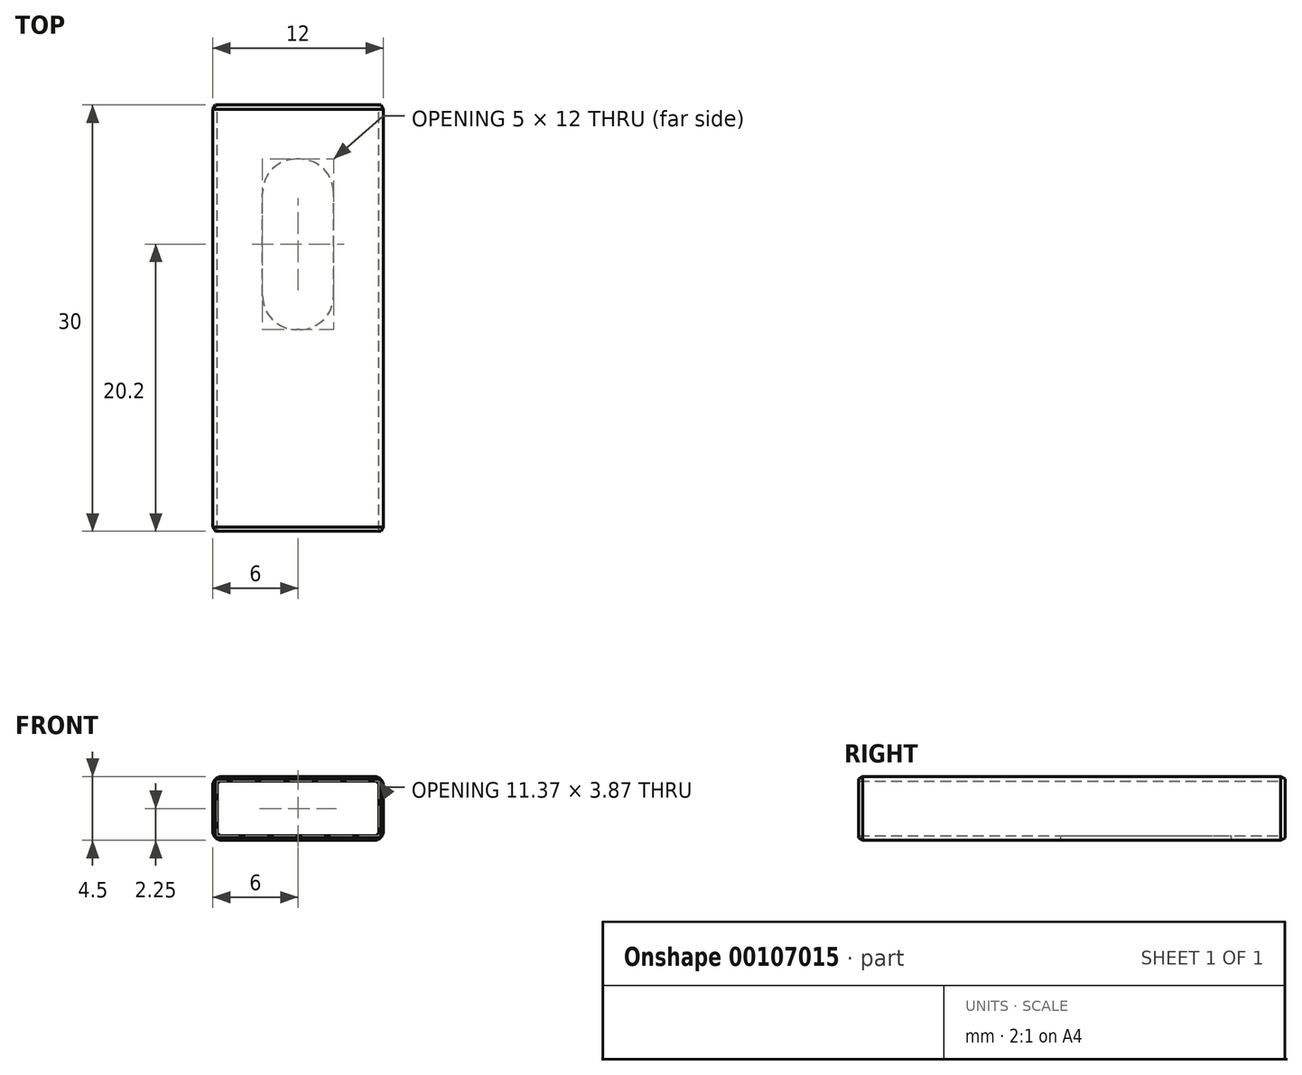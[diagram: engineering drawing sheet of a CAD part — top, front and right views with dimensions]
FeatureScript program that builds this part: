
annotation { "Feature Type Name" : "Feature", "Feature Type Description" : "" }
export const myFeature = defineFeature(function(context is Context, id is Id, definition is map)
    precondition{}
    {
        {
            var Q0;
            Q0=qCreatedBy(makeId("Front.planeOp"),FACE);
            var sketch = newSketch(context, id + "F0", { "sketchPlane" : qUnion([Q0])});
            skLineSegment(sketch, "E0.bottom", {"start": v(0.64, 0) * mm, "end": v(11.36, 0) * mm});
            skLineSegment(sketch, "E0.top", {"start": v(0.64, 4.5) * mm, "end": v(11.36, 4.5) * mm});
            skLineSegment(sketch, "E0.left", {"start": v(0, 0.64) * mm, "end": v(0, 3.86) * mm});
            skLineSegment(sketch, "E0.right", {"start": v(12, 0.64) * mm, "end": v(12, 3.86) * mm});
            skPoint(sketch, "E1.visualSharp", {"position": v(0, 4.5) * mm});
            skArc(sketch, "E1.filletArc", {"start": v(0.64, 4.5) * mm, "mid": v(0.19, 4.31) * mm, "end": v(0, 3.86) * mm});
            skPoint(sketch, "E2.visualSharp", {"position": v(12, 4.5) * mm});
            skArc(sketch, "E2.filletArc", {"start": v(12, 3.86) * mm, "mid": v(11.81, 4.31) * mm, "end": v(11.36, 4.5) * mm});
            skPoint(sketch, "E3.visualSharp", {"position": v(12, 0) * mm});
            skArc(sketch, "E3.filletArc", {"start": v(11.36, 0) * mm, "mid": v(11.81, 0.19) * mm, "end": v(12, 0.64) * mm});
            skPoint(sketch, "E4.visualSharp", {"position": v(0, 0) * mm});
            skArc(sketch, "E4.filletArc", {"start": v(0, 0.64) * mm, "mid": v(0.19, 0.19) * mm, "end": v(0.64, 0) * mm});
            skArc(sketch, "E5.0", {"start": v(0.64, 4.19) * mm, "mid": v(0.41, 4.09) * mm, "end": v(0.31, 3.86) * mm});
            skLineSegment(sketch, "E5.1", {"start": v(0.32, 0.64) * mm, "end": v(0.31, 3.86) * mm});
            skLineSegment(sketch, "E5.2", {"start": v(0.64, 4.19) * mm, "end": v(11.36, 4.19) * mm});
            skArc(sketch, "E5.3", {"start": v(0.32, 0.64) * mm, "mid": v(0.41, 0.41) * mm, "end": v(0.64, 0.32) * mm});
            skArc(sketch, "E5.4", {"start": v(11.69, 3.86) * mm, "mid": v(11.59, 4.09) * mm, "end": v(11.36, 4.19) * mm});
            skLineSegment(sketch, "E5.5", {"start": v(11.69, 0.64) * mm, "end": v(11.69, 3.86) * mm});
            skArc(sketch, "E5.6", {"start": v(11.36, 0.31) * mm, "mid": v(11.59, 0.41) * mm, "end": v(11.69, 0.64) * mm});
            skLineSegment(sketch, "E5.7", {"start": v(0.64, 0.32) * mm, "end": v(11.36, 0.32) * mm});
            skSolve(sketch);
        }
        {
            var Q0;
            Q0 = qSketchRegion(id + "F0", true);
            extrude(context, id + "F1", {"entities" : qUnion([Q0]), "depth" : 30 * mm});
        }
        {
            var Q0;
            Q0=makeQuery(id+"F1.opExtrude","SWEPT_FACE",FACE,{"disambiguationData":[OSD([sQuery(id+"F0.wireOp",EDGE,"E0.bottom")])]});
            var sketch = newSketch(context, id + "F2", { "sketchPlane" : qUnion([Q0])});
            skLineSegment(sketch, "E6.bottom", {"start": v(6.1, 15.8) * mm, "end": v(5.9, 15.8) * mm});
            skLineSegment(sketch, "E6.top", {"start": v(6.1, 3.8) * mm, "end": v(5.9, 3.8) * mm});
            skLineSegment(sketch, "E6.left", {"start": v(8.5, 13.4) * mm, "end": v(8.5, 6.2) * mm});
            skLineSegment(sketch, "E6.right", {"start": v(3.5, 13.4) * mm, "end": v(3.5, 6.2) * mm});
            skPoint(sketch, "E7.visualSharp", {"position": v(8.5, 15.8) * mm});
            skArc(sketch, "E7.filletArc", {"start": v(8.5, 13.4) * mm, "mid": v(7.8, 15.1) * mm, "end": v(6.1, 15.8) * mm});
            skPoint(sketch, "E8.visualSharp", {"position": v(3.5, 3.8) * mm});
            skArc(sketch, "E8.filletArc", {"start": v(3.5, 6.2) * mm, "mid": v(4.2, 4.5) * mm, "end": v(5.9, 3.8) * mm});
            skPoint(sketch, "E9.visualSharp", {"position": v(8.5, 3.8) * mm});
            skArc(sketch, "E9.filletArc", {"start": v(6.1, 3.8) * mm, "mid": v(7.8, 4.5) * mm, "end": v(8.5, 6.2) * mm});
            skPoint(sketch, "E10.visualSharp", {"position": v(3.5, 15.8) * mm});
            skArc(sketch, "E10.filletArc", {"start": v(5.9, 15.8) * mm, "mid": v(4.2, 15.1) * mm, "end": v(3.5, 13.4) * mm});
            skSolve(sketch);
        }
        {
            var Q0;
            Q0 = qSketchRegion(id + "F2", true);
            extrude(context, id + "F3", {"entities" : qUnion([Q0]), "operationType" : NewBodyOperationType.REMOVE, "endBound" : BoundingType.UP_TO_NEXT, "oppositeDirection" : true, "depth" : 25 * mm});
        }
        {
            var Q0;
            Q0=makeQuery(id+"F1.opExtrude","CAP_EDGE",EDGE,{"disambiguationData":[OSD([sQuery(id+"F0.wireOp",EDGE,"E0.bottom")])],"isStart":true});
            var Q1;
            Q1=makeQuery(id+"F1.opExtrude","CAP_EDGE",EDGE,{"disambiguationData":[OSD([sQuery(id+"F0.wireOp",EDGE,"E0.bottom")])],"isStart":false});
            chamfer(context, id + "F4", {"entities" : qUnion([Q0, Q1]), "chamferType" : ChamferType.OFFSET_ANGLE, "width" : .3 * mm, "oppositeDirection" : false, "angle" : 30 * degree, "tangentPropagation" : true});
        }
    });
